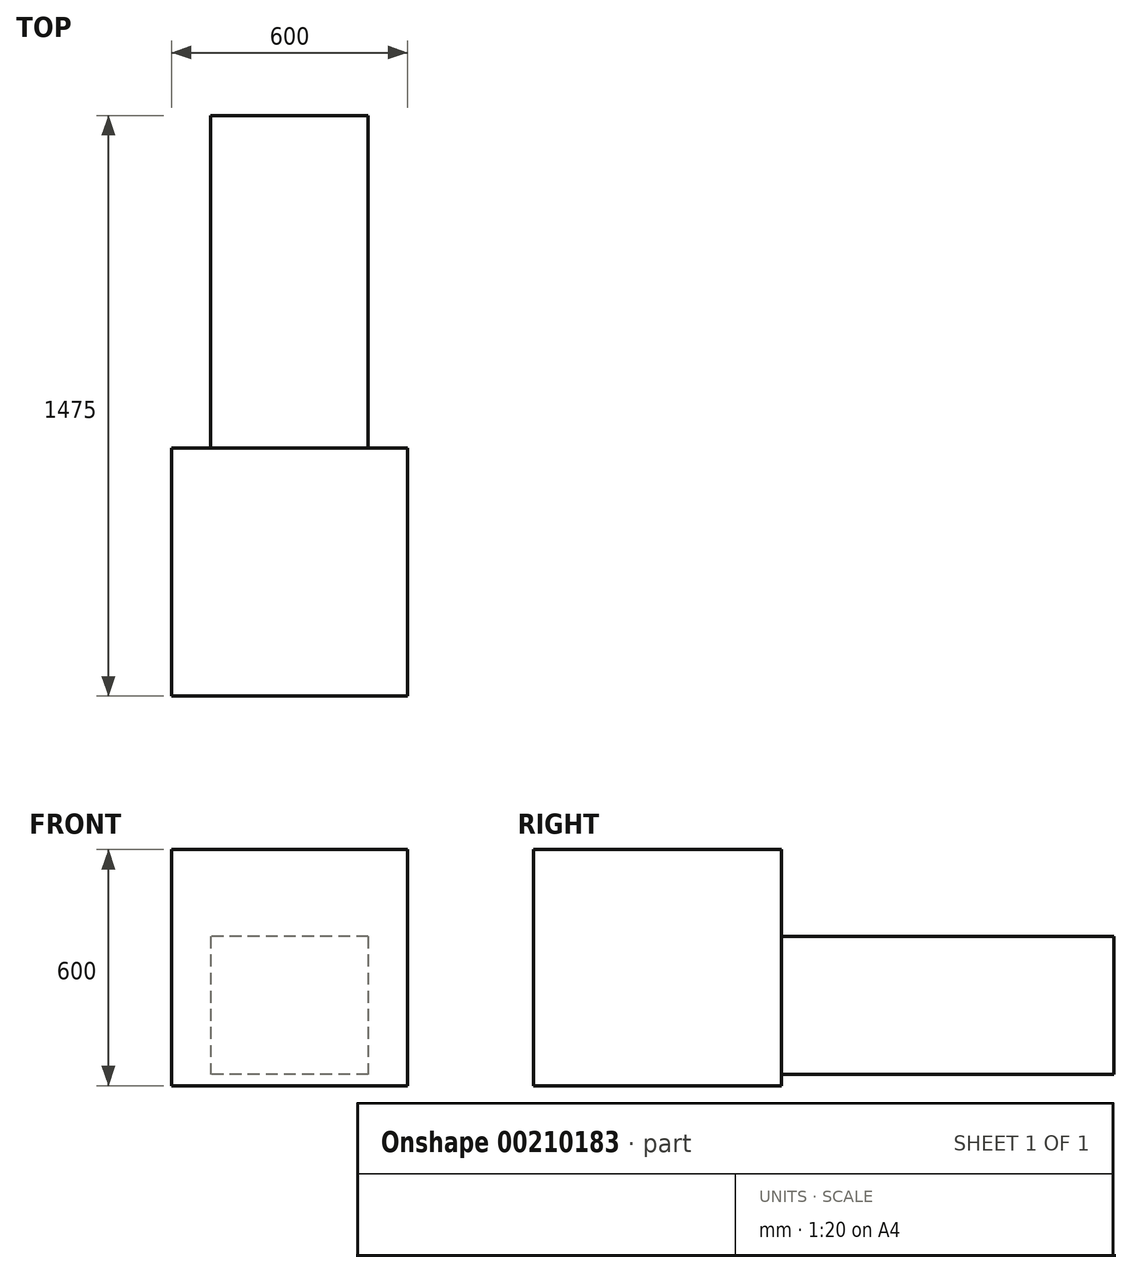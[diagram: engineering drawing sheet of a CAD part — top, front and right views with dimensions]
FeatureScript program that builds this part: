
annotation { "Feature Type Name" : "Feature", "Feature Type Description" : "" }
export const myFeature = defineFeature(function(context is Context, id is Id, definition is map)
    precondition{}
    {
        {
            var Q0;
            Q0=qCreatedBy(makeId("Front.planeOp"),FACE);
            var sketch = newSketch(context, id + "F0", { "sketchPlane" : qUnion([Q0])});
            skLineSegment(sketch, "E0.bottom", {"start": v(-300, 0) * mm, "end": v(300, 0) * mm});
            skLineSegment(sketch, "E0.top", {"start": v(-300, 600) * mm, "end": v(300, 600) * mm});
            skLineSegment(sketch, "E0.left", {"start": v(-300, 0) * mm, "end": v(-300, 600) * mm});
            skLineSegment(sketch, "E0.right", {"start": v(300, 0) * mm, "end": v(300, 600) * mm});
            skSolve(sketch);
        }
        {
            var Q0;
            Q0=makeQuery(id+"F0.imprint","IMPRINT",FACE,{"disambiguationData":[TD([[makeQuery(id+"F0.imprint","IMPRINT",EDGE,{"derivedFrom":sQuery(id+"F0.wireOp",EDGE,"E0.bottom")}),1.0]])]});
            extrude(context, id + "F1", {"entities" : qUnion([Q0]), "depth" : 630 * mm});
        }
        {
            var Q0;
            Q0=qCreatedBy(makeId("Right.planeOp"),FACE);
            var sketch = newSketch(context, id + "F2", { "sketchPlane" : qUnion([Q0])});
            skLineSegment(sketch, "E1.bottom", {"start": v(0, 378.94) * mm, "end": v(845, 378.94) * mm});
            skLineSegment(sketch, "E1.top", {"start": v(0, 28.94) * mm, "end": v(845, 28.94) * mm});
            skLineSegment(sketch, "E1.left", {"start": v(0, 378.94) * mm, "end": v(0, 28.94) * mm});
            skLineSegment(sketch, "E1.right", {"start": v(845, 378.94) * mm, "end": v(845, 28.94) * mm});
            skSolve(sketch);
        }
        {
            var Q0;
            Q0=makeQuery(id+"F2.imprint","IMPRINT",FACE,{"disambiguationData":[TD([[makeQuery(id+"F2.imprint","IMPRINT",EDGE,{"derivedFrom":sQuery(id+"F2.wireOp",EDGE,"E1.bottom")}),-1.0]])]});
            extrude(context, id + "F3", {"entities" : qUnion([Q0]), "operationType" : NewBodyOperationType.ADD, "depth" : 200 * mm, "hasSecondDirection" : true, "secondDirectionOppositeDirection" : true, "secondDirectionDepth" : 200 * mm});
        }
    });
